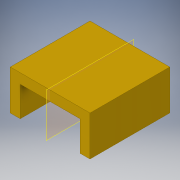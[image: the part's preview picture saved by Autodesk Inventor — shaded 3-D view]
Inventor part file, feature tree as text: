
AUTODESK INVENTOR PART (.ipt)
format: ipt  version: 2017 (Build 210142000, 142)  size: 120,320 bytes
history: native  units: in
note: dims shown in document units (in); Inventor stores cm internally (conversion verified against a paired STEP export)
features: sketch x3, extrude x2, plane x1
ambient origin geometry x8: Origin, YZ Plane, XZ Plane, XY Plane, X Axis, Y Axis, Z Axis, Center Point
bodies: Solid1 (feature_tree)
feature tree (6):
  sketch  "Sketch1"  dims[d0=0.25in d1=0.25in]
  extrude  "Extrusion1"  Depth=0.25in
  plane  "Work Plane1"
  extrude  "Extrusion2"  Depth=1.5in
  sketch  "Sketch2"  dims[d2=0.25in d3=1.5in]
  sketch  "Sketch4"  dims[d4=1.0in d5=2.0in d6=0.0in d13=0.13in d14=0.125in d15=0.25in d16=0.13in d17=0.25in d18=0.5in d19=0.0in]
